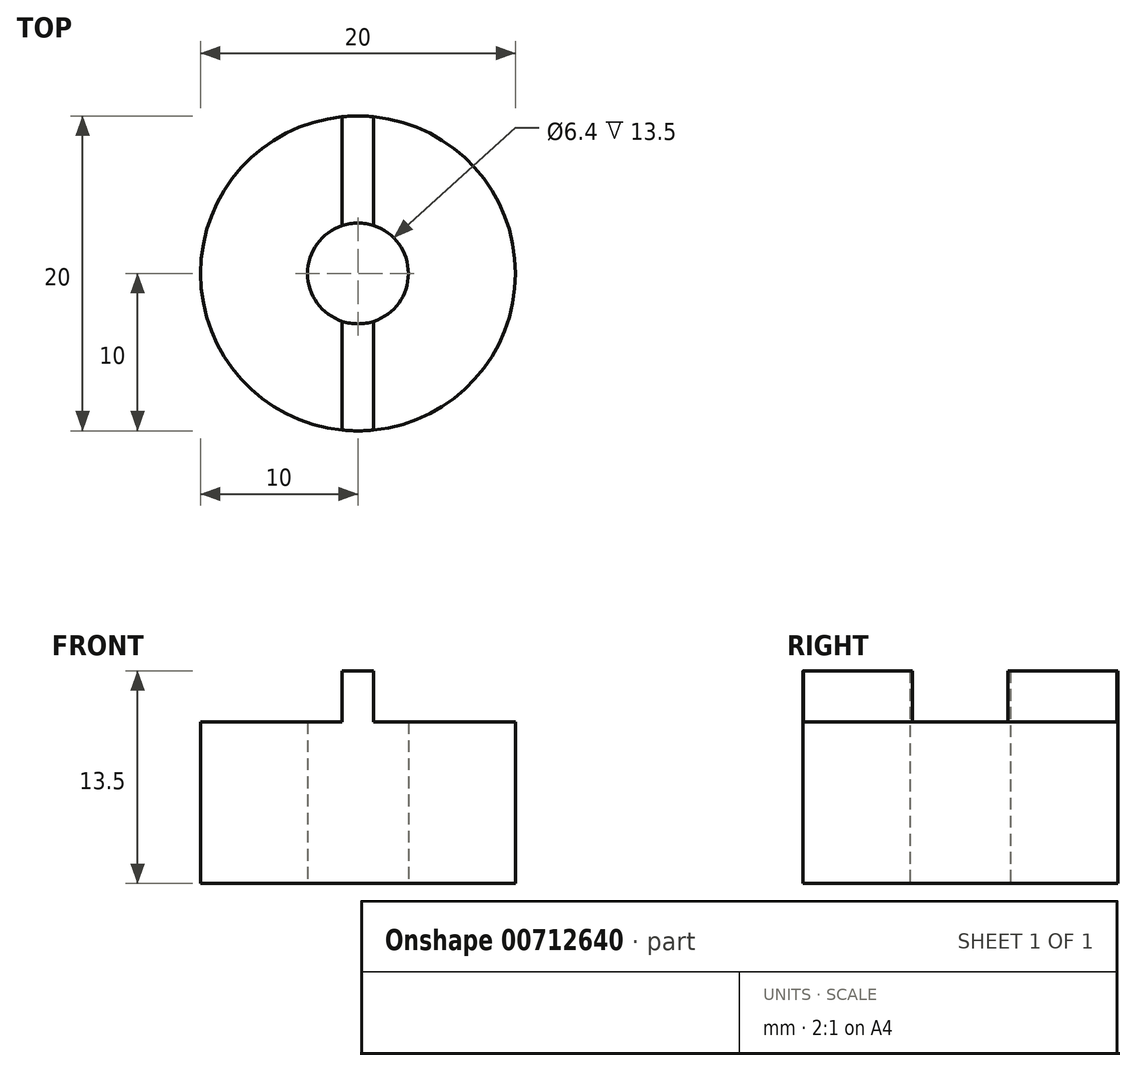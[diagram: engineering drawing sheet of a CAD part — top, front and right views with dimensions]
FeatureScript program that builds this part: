
annotation { "Feature Type Name" : "Feature", "Feature Type Description" : "" }
export const myFeature = defineFeature(function(context is Context, id is Id, definition is map)
    precondition{}
    {
        {
            var Q0;
            Q0=qCreatedBy(makeId("Top.planeOp"),FACE);
            var sketch = newSketch(context, id + "F0", { "sketchPlane" : qUnion([Q0])});
            skCircle(sketch, "E0", {"center": v(0, 0) * mm, "radius": 3.2 * mm});
            skCircle(sketch, "E1", {"center": v(0, 0) * mm, "radius": 10 * mm});
            skSolve(sketch);
        }
        {
            var Q0;
            Q0=qCreatedBy(makeId("Front.planeOp"),FACE);
            var sketch = newSketch(context, id + "F1", { "sketchPlane" : qUnion([Q0])});
            skLineSegment(sketch, "E2.bottom", {"start": v(-1, 12.5) * mm, "end": v(1, 12.5) * mm});
            skLineSegment(sketch, "E2.top", {"start": v(-3, 0) * mm, "end": v(3, 0) * mm});
            skPoint(sketch, "E3", {"position": v(0, 0) * mm});
            skLineSegment(sketch, "E4", {"start": v(-1, 12.5) * mm, "end": v(-1, 10.25) * mm});
            skLineSegment(sketch, "E5", {"start": v(-1, 10.25) * mm, "end": v(-3, 10.25) * mm});
            skLineSegment(sketch, "E6", {"start": v(-3, 10.25) * mm, "end": v(-3, 0) * mm});
            skLineSegment(sketch, "E7", {"start": v(3, 10.25) * mm, "end": v(3, 0) * mm});
            skLineSegment(sketch, "E8", {"start": v(3, 10.25) * mm, "end": v(1, 10.25) * mm});
            skLineSegment(sketch, "E9", {"start": v(1, 10.25) * mm, "end": v(1, 12.5) * mm});
            skLineSegment(sketch, "E10", {"start": v(-1, 10.25) * mm, "end": v(1, 10.25) * mm});
            skLineSegment(sketch, "E11", {"start": v(0, 12.75) * mm, "end": v(0, 0) * mm, "construction": true});
            skLineSegment(sketch, "E12", {"start": v(0, 12.75) * mm, "end": v(0, 12.5) * mm});
            skLineSegment(sketch, "E13.top", {"start": v(-3, 10.25) * mm, "end": v(-10.77, 10.25) * mm});
            skLineSegment(sketch, "E13.right", {"start": v(-10.77, 12.5) * mm, "end": v(-10.77, 10.25) * mm});
            skLineSegment(sketch, "E14.top", {"start": v(3, 10.25) * mm, "end": v(10.74, 10.25) * mm});
            skLineSegment(sketch, "E14.right", {"start": v(10.74, 12.5) * mm, "end": v(10.74, 10.25) * mm});
            skLineSegment(sketch, "E15.top", {"start": v(1, 15.12) * mm, "end": v(10.74, 15.12) * mm});
            skLineSegment(sketch, "E15.left", {"start": v(1, 12.5) * mm, "end": v(1, 15.12) * mm});
            skLineSegment(sketch, "E15.right", {"start": v(10.74, 12.5) * mm, "end": v(10.74, 15.12) * mm});
            skLineSegment(sketch, "E16.top", {"start": v(-10.77, 15.12) * mm, "end": v(-1, 15.12) * mm});
            skLineSegment(sketch, "E16.left", {"start": v(-10.77, 12.5) * mm, "end": v(-10.77, 15.12) * mm});
            skLineSegment(sketch, "E16.right", {"start": v(-1, 12.5) * mm, "end": v(-1, 15.12) * mm});
            skPoint(sketch, "E17", {"position": v(-1, 12.75) * mm});
            skSolve(sketch);
        }
        {
            var Q0;
            Q0=makeQuery(id+"F0.imprint","IMPRINT",FACE,{"disambiguationData":[TD([[makeQuery(id+"F0.imprint","IMPRINT",EDGE,{"derivedFrom":sQuery(id+"F0.wireOp",EDGE,"E0")}),-1.0]])]});
            extrude(context, id + "F2", {"entities" : qUnion([Q0]), "depth" : 13.5 * mm, "offsetDistance" : 25 * mm});
        }
        {
            var Q0;
            Q0=makeQuery(id+"F1.imprint","IMPRINT",FACE,{"disambiguationData":[TD([[makeQuery(id+"F1.imprint","IMPRINT",EDGE,{"derivedFrom":sQuery(id+"F1.wireOp",EDGE,"E4")}),-1.0]])]});
            var Q1;
            Q1=makeQuery(id+"F1.imprint","IMPRINT",FACE,{"disambiguationData":[TD([[makeQuery(id+"F1.imprint","IMPRINT",EDGE,{"derivedFrom":sQuery(id+"F1.wireOp",EDGE,"E8")}),-1.0]])]});
            extrude(context, id + "F3", {"entities" : qUnion([Q0, Q1]), "operationType" : NewBodyOperationType.REMOVE, "oppositeDirection" : true, "depth" : 25 * mm, "offsetDistance" : 25 * mm});
        }
        {
            var Q0;
            Q0=makeQuery(id+"F1.imprint","IMPRINT",FACE,{"disambiguationData":[TD([[makeQuery(id+"F1.imprint","IMPRINT",EDGE,{"derivedFrom":sQuery(id+"F1.wireOp",EDGE,"E4")}),-1.0]])]});
            var Q1;
            Q1=makeQuery(id+"F1.imprint","IMPRINT",FACE,{"disambiguationData":[TD([[makeQuery(id+"F1.imprint","IMPRINT",EDGE,{"derivedFrom":sQuery(id+"F1.wireOp",EDGE,"E8")}),-1.0]])]});
            extrude(context, id + "F4", {"entities" : qUnion([Q0, Q1]), "operationType" : NewBodyOperationType.REMOVE, "depth" : 11.4 * mm, "offsetDistance" : 25 * mm});
        }
    });
